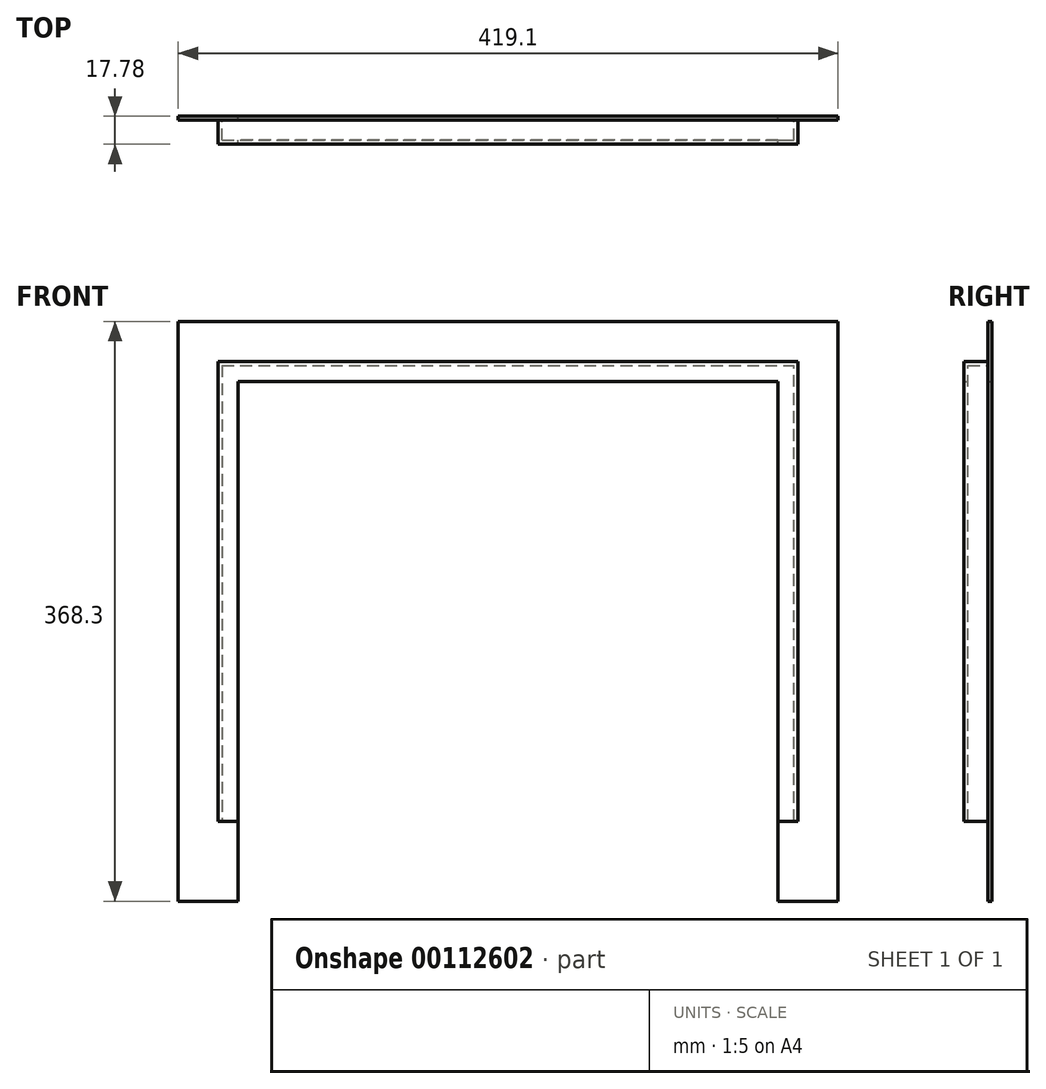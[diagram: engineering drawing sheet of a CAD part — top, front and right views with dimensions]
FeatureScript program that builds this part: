
annotation { "Feature Type Name" : "Feature", "Feature Type Description" : "" }
export const myFeature = defineFeature(function(context is Context, id is Id, definition is map)
    precondition{}
    {
        {
            var Q0;
            Q0=qCreatedBy(makeId("Front.planeOp"),FACE);
            var sketch = newSketch(context, id + "F0", { "sketchPlane" : qUnion([Q0])});
            skLineSegment(sketch, "E0", {"start": v(0, -279.4) * mm, "end": v(0, 0) * mm});
            skLineSegment(sketch, "E1", {"start": v(-12.7, -279.4) * mm, "end": v(0, -279.4) * mm});
            skLineSegment(sketch, "E2", {"start": v(-12.7, 12.7) * mm, "end": v(-12.7, -279.4) * mm});
            skLineSegment(sketch, "E3", {"start": v(-12.7, 12.7) * mm, "end": v(355.6, 12.7) * mm});
            skLineSegment(sketch, "E4", {"start": v(355.6, -279.4) * mm, "end": v(355.6, 12.7) * mm});
            skLineSegment(sketch, "E5", {"start": v(342.9, -279.4) * mm, "end": v(355.6, -279.4) * mm});
            skLineSegment(sketch, "E6", {"start": v(342.9, 0) * mm, "end": v(342.9, -279.4) * mm});
            skLineSegment(sketch, "E7", {"start": v(342.9, 0) * mm, "end": v(0, 0) * mm});
            skSolve(sketch);
        }
        {
            var Q0;
            Q0 = qSketchRegion(id + "F0", true);
            extrude(context, id + "F1", {"entities" : qUnion([Q0]), "endBound" : BoundingType.SYMMETRIC, "depth" : 17.78 * mm});
        }
        {
            var Q0;
            Q0=makeQuery(id+"F1.opExtrude","SWEPT_FACE",FACE,{"disambiguationData":[OSD([sQuery(id+"F0.wireOp",EDGE,"E7")])]});
            var Q1;
            Q1=makeQuery(id+"F1.opExtrude","SWEPT_FACE",FACE,{"disambiguationData":[OSD([sQuery(id+"F0.wireOp",EDGE,"E0")])]});
            var Q2;
            Q2=makeQuery(id+"F1.opExtrude","SWEPT_FACE",FACE,{"disambiguationData":[OSD([sQuery(id+"F0.wireOp",EDGE,"E1")])]});
            var Q3;
            Q3=makeQuery(id+"F1.opExtrude","SWEPT_FACE",FACE,{"disambiguationData":[OSD([sQuery(id+"F0.wireOp",EDGE,"E6")])]});
            var Q4;
            Q4=makeQuery(id+"F1.opExtrude","SWEPT_FACE",FACE,{"disambiguationData":[OSD([sQuery(id+"F0.wireOp",EDGE,"E5")])]});
            shell(context, id + "F2", {"entities" : qUnion([Q0, Q1, Q2, Q3, Q4]), "thickness" : 2.54 * mm});
        }
        {
            var Q0;
            Q0=makeQuery(id+"F1.opExtrude","CAP_FACE",FACE,{"disambiguationData":[OSD([sQuery(id+"F0.wireOp",EDGE,"E0"),sQuery(id+"F0.wireOp",EDGE,"E1"),sQuery(id+"F0.wireOp",EDGE,"E2"),sQuery(id+"F0.wireOp",EDGE,"E3"),sQuery(id+"F0.wireOp",EDGE,"E4"),sQuery(id+"F0.wireOp",EDGE,"E5"),sQuery(id+"F0.wireOp",EDGE,"E6"),sQuery(id+"F0.wireOp",EDGE,"E7")])],"isStart":true});
            var sketch = newSketch(context, id + "F3", { "sketchPlane" : qUnion([Q0])});
            skLineSegment(sketch, "E8", {"start": v(-381, -330.2) * mm, "end": v(-381, 38.1) * mm});
            skLineSegment(sketch, "E9", {"start": v(-381, 38.1) * mm, "end": v(38.1, 38.1) * mm});
            skLineSegment(sketch, "E10", {"start": v(-342.9, -279.4) * mm, "end": v(-342.9, 0) * mm});
            skLineSegment(sketch, "E11", {"start": v(-342.9, 0) * mm, "end": v(0, 0) * mm});
            skLineSegment(sketch, "E12", {"start": v(-381, -330.2) * mm, "end": v(-342.9, -330.2) * mm});
            skLineSegment(sketch, "E13", {"start": v(38.1, -330.2) * mm, "end": v(38.1, 38.1) * mm});
            skLineSegment(sketch, "E14", {"start": v(0, -279.4) * mm, "end": v(0, -330.2) * mm});
            skLineSegment(sketch, "E15", {"start": v(-342.9, -279.4) * mm, "end": v(-342.9, -330.2) * mm});
            skLineSegment(sketch, "E16.trimOffspring", {"start": v(0, -330.2) * mm, "end": v(38.1, -330.2) * mm});
            skSolve(sketch);
        }
        {
            var Q0;
            Q0=makeQuery(id+"F3.imprint","IMPRINT",FACE,{"disambiguationData":[TD([[makeQuery(id+"F3.imprint","IMPRINT",EDGE,{"derivedFrom":sQuery(id+"F3.wireOp",EDGE,"E8")}),-1.0]])]});
            extrude(context, id + "F4", {"entities" : qUnion([Q0]), "operationType" : NewBodyOperationType.ADD, "oppositeDirection" : true, "depth" : 2.54 * mm});
        }
    });
